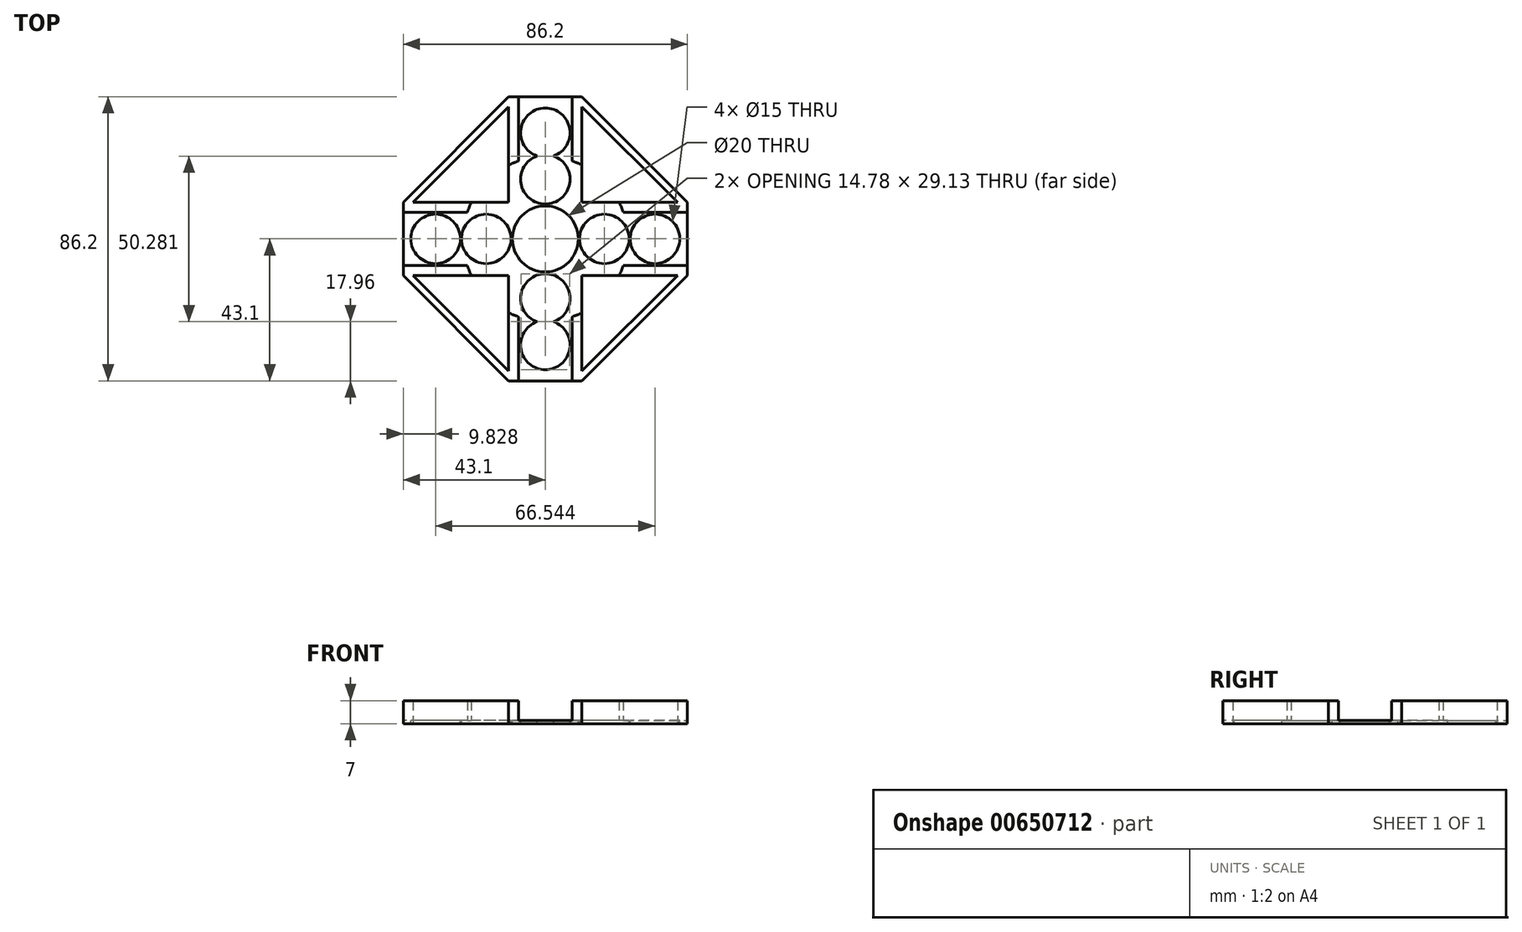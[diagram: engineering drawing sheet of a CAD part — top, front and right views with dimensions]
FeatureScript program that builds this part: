
annotation { "Feature Type Name" : "Feature", "Feature Type Description" : "" }
export const myFeature = defineFeature(function(context is Context, id is Id, definition is map)
    precondition{}
    {
        {
            var Q0;
            Q0=qCreatedBy(makeId("Top.planeOp"),FACE);
            var sketch = newSketch(context, id + "F0", { "sketchPlane" : qUnion([Q0])});
            skLineSegment(sketch, "E0.bottom", {"start": v(8.1, -64.67) * mm, "end": v(-8.1, -64.67) * mm, "construction": true});
            skLineSegment(sketch, "E0.top", {"start": v(8.1, 64.67) * mm, "end": v(-8.1, 64.67) * mm, "construction": true});
            skLineSegment(sketch, "E0.left", {"start": v(8.1, -64.67) * mm, "end": v(8.1, 64.67) * mm, "construction": true});
            skLineSegment(sketch, "E0.right", {"start": v(-8.1, -64.67) * mm, "end": v(-8.1, 64.67) * mm, "construction": true});
            skPoint(sketch, "E0.middle", {"position": v(0, 0) * mm});
            skLineSegment(sketch, "E1.bottom", {"start": v(98.4, -8.1) * mm, "end": v(-98.4, -8.1) * mm, "construction": true});
            skLineSegment(sketch, "E1.top", {"start": v(98.4, 8.1) * mm, "end": v(-98.4, 8.1) * mm, "construction": true});
            skLineSegment(sketch, "E1.left", {"start": v(98.4, -8.1) * mm, "end": v(98.4, 8.1) * mm, "construction": true});
            skLineSegment(sketch, "E1.right", {"start": v(-98.4, -8.1) * mm, "end": v(-98.4, 8.1) * mm, "construction": true});
            skLineSegment(sketch, "E2.bottom", {"start": v(11.1, -18.1) * mm, "end": v(-11.1, -18.1) * mm});
            skLineSegment(sketch, "E2.top", {"start": v(11.1, 18.1) * mm, "end": v(-11.1, 18.1) * mm});
            skLineSegment(sketch, "E2.left", {"start": v(11.1, -18.1) * mm, "end": v(11.1, -11.1) * mm});
            skLineSegment(sketch, "E2.right", {"start": v(-11.1, -18.1) * mm, "end": v(-11.1, -11.1) * mm});
            skLineSegment(sketch, "E3.bottom", {"start": v(18.1, -11.1) * mm, "end": v(11.1, -11.1) * mm});
            skLineSegment(sketch, "E3.top", {"start": v(18.1, 11.1) * mm, "end": v(11.1, 11.1) * mm});
            skLineSegment(sketch, "E3.left", {"start": v(18.1, -11.1) * mm, "end": v(18.1, 11.1) * mm});
            skLineSegment(sketch, "E3.right", {"start": v(-18.1, -11.1) * mm, "end": v(-18.1, 11.1) * mm});
            skLineSegment(sketch, "E4.trimOffspring", {"start": v(-11.1, 11.1) * mm, "end": v(-11.1, 18.1) * mm});
            skLineSegment(sketch, "E5.trimOffspring", {"start": v(11.1, 11.1) * mm, "end": v(11.1, 18.1) * mm});
            skLineSegment(sketch, "E6.trimOffspring", {"start": v(-11.1, -11.1) * mm, "end": v(-18.1, -11.1) * mm});
            skLineSegment(sketch, "E7.trimOffspring", {"start": v(-11.1, 11.1) * mm, "end": v(-18.1, 11.1) * mm});
            skSolve(sketch);
        }
        {
            var Q0;
            Q0 = qSketchRegion(id + "F0", true);
            var Q1;
            Q1=makeQuery(id+"F0.imprint","IMPRINT",FACE,{"disambiguationData":[TD([[makeQuery(id+"F0.imprint","IMPRINT",EDGE,{"derivedFrom":sQuery(id+"F0.wireOp",EDGE,"E2.bottom")}),-1.0]])]});
            extrude(context, id + "F1", {"entities" : qUnion([Q0, Q1]), "depth" : 1 * mm, "offsetDistance" : 25 * mm});
        }
        {
            var Q0;
            Q0=makeQuery(id+"F1.opExtrude","CAP_FACE",FACE,{"disambiguationData":[OSD([sQuery(id+"F0.wireOp",EDGE,"E2.bottom"),sQuery(id+"F0.wireOp",EDGE,"E2.top"),sQuery(id+"F0.wireOp",EDGE,"E2.left"),sQuery(id+"F0.wireOp",EDGE,"E2.right"),sQuery(id+"F0.wireOp",EDGE,"E3.bottom"),sQuery(id+"F0.wireOp",EDGE,"E3.top"),sQuery(id+"F0.wireOp",EDGE,"E3.left"),sQuery(id+"F0.wireOp",EDGE,"E3.right"),sQuery(id+"F0.wireOp",EDGE,"E4.trimOffspring"),sQuery(id+"F0.wireOp",EDGE,"E5.trimOffspring"),sQuery(id+"F0.wireOp",EDGE,"E6.trimOffspring"),sQuery(id+"F0.wireOp",EDGE,"E7.trimOffspring")])],"isStart":false});
            var sketch = newSketch(context, id + "F2", { "sketchPlane" : qUnion([Q0])});
            skLineSegment(sketch, "E8.0", {"start": v(-8.1, -64.67) * mm, "end": v(-8.1, 64.67) * mm, "construction": true});
            skLineSegment(sketch, "E8.1", {"start": v(98.4, 8.1) * mm, "end": v(-98.4, 8.1) * mm, "construction": true});
            skLineSegment(sketch, "E8.2", {"start": v(98.4, -8.1) * mm, "end": v(-98.4, -8.1) * mm, "construction": true});
            skLineSegment(sketch, "E8.3", {"start": v(8.1, -64.67) * mm, "end": v(8.1, 64.67) * mm, "construction": true});
            skLineSegment(sketch, "E9", {"start": v(-8.1, 8.1) * mm, "end": v(-8.1, 18.1) * mm});
            skLineSegment(sketch, "E10", {"start": v(-8.1, 8.1) * mm, "end": v(-18.1, 8.1) * mm});
            skLineSegment(sketch, "E11", {"start": v(8.1, 8.1) * mm, "end": v(18.1, 8.1) * mm});
            skLineSegment(sketch, "E12", {"start": v(8.1, 18.1) * mm, "end": v(8.1, 8.1) * mm});
            skLineSegment(sketch, "E13", {"start": v(-8.1, -8.1) * mm, "end": v(-8.1, -18.1) * mm});
            skLineSegment(sketch, "E14", {"start": v(-18.1, -8.1) * mm, "end": v(-8.1, -8.1) * mm});
            skLineSegment(sketch, "E15", {"start": v(8.1, -8.1) * mm, "end": v(18.1, -8.1) * mm});
            skLineSegment(sketch, "E16", {"start": v(8.1, -8.1) * mm, "end": v(8.1, -18.1) * mm});
            skSolve(sketch);
        }
        {
            var Q0;
            {var subQ4=sQuery(id+"F2.wireOp",EDGE,"E9");Q0=makeQuery(id+"F2.imprint","IMPRINT",FACE,{"disambiguationData":[TD([[makeQuery(id+"F2.imprint","IMPRINT",EDGE,{"derivedFrom":subQ4}),1.0]])]});}
            var Q1;
            {var subQ2=sQuery(id+"F2.wireOp",EDGE,"E11");Q1=makeQuery(id+"F2.imprint","IMPRINT",FACE,{"disambiguationData":[TD([[makeQuery(id+"F2.imprint","IMPRINT",EDGE,{"derivedFrom":subQ2}),1.0]])]});}
            var Q2;
            {var subQ3=sQuery(id+"F2.wireOp",EDGE,"E15");Q2=makeQuery(id+"F2.imprint","IMPRINT",FACE,{"disambiguationData":[TD([[makeQuery(id+"F2.imprint","IMPRINT",EDGE,{"derivedFrom":subQ3}),-1.0]])]});}
            var Q3;
            {var subQ4=sQuery(id+"F2.wireOp",EDGE,"E13");Q3=makeQuery(id+"F2.imprint","IMPRINT",FACE,{"disambiguationData":[TD([[makeQuery(id+"F2.imprint","IMPRINT",EDGE,{"derivedFrom":subQ4}),-1.0]])]});}
            extrude(context, id + "F3", {"entities" : qUnion([Q0, Q1, Q2, Q3]), "operationType" : NewBodyOperationType.ADD, "depth" : 6 * mm, "offsetDistance" : 25 * mm});
        }
        {
            var Q0;
            {var subQ0=sQuery(id+"F0.wireOp",EDGE,"E3.right");var subQ1=makeQuery(id+"F1.opExtrude","CAP_EDGE",EDGE,{"disambiguationData":[OSD([subQ0])],"isStart":false});Q0=makeQuery(id+"F3.boolean.opBoolean","MERGE",FACE,{"derivedFrom":[makeQuery(id+"F1.opExtrude","SWEPT_FACE",FACE,{"disambiguationData":[OSD([subQ0])]}),makeQuery(id+"F3.opExtrude","SWEPT_FACE",FACE,{"disambiguationData":[OSD([subQ0]),TDD([makeQuery(id+"F2.imprint","IMPRINT",EDGE,{"disambiguationData":[TD([[makeQuery(id+"F2.imprint","INTERSECT",VERTEX,{"derivedFrom":[subQ1,makeQuery(id+"F1.opExtrude","CAP_EDGE",EDGE,{"disambiguationData":[OSD([sQuery(id+"F0.wireOp",EDGE,"E6.trimOffspring")])],"isStart":false})]}),-1.0]])],"derivedFrom":subQ1})])]}),makeQuery(id+"F3.opExtrude","SWEPT_FACE",FACE,{"disambiguationData":[OSD([subQ0]),TDD([makeQuery(id+"F2.imprint","IMPRINT",EDGE,{"disambiguationData":[TD([[makeQuery(id+"F2.imprint","INTERSECT",VERTEX,{"derivedFrom":[subQ1,makeQuery(id+"F1.opExtrude","CAP_EDGE",EDGE,{"disambiguationData":[OSD([sQuery(id+"F0.wireOp",EDGE,"E7.trimOffspring")])],"isStart":false})]}),1.0]])],"derivedFrom":subQ1})])]})]});}
            extrude(context, id + "F4", {"entities" : qUnion([Q0]), "operationType" : NewBodyOperationType.ADD, "depth" : 25 * mm, "offsetDistance" : 25 * mm});
        }
        {
            var Q0;
            {var subQ0=sQuery(id+"F0.wireOp",EDGE,"E3.left");var subQ1=makeQuery(id+"F1.opExtrude","CAP_EDGE",EDGE,{"disambiguationData":[OSD([subQ0])],"isStart":false});Q0=makeQuery(id+"F3.boolean.opBoolean","MERGE",FACE,{"derivedFrom":[makeQuery(id+"F1.opExtrude","SWEPT_FACE",FACE,{"disambiguationData":[OSD([subQ0])]}),makeQuery(id+"F3.opExtrude","SWEPT_FACE",FACE,{"disambiguationData":[OSD([subQ0]),TDD([makeQuery(id+"F2.imprint","IMPRINT",EDGE,{"disambiguationData":[TD([[makeQuery(id+"F2.imprint","INTERSECT",VERTEX,{"derivedFrom":[makeQuery(id+"F1.opExtrude","CAP_EDGE",EDGE,{"disambiguationData":[OSD([sQuery(id+"F0.wireOp",EDGE,"E3.bottom")])],"isStart":false}),subQ1]}),-1.0]])],"derivedFrom":subQ1})])]}),makeQuery(id+"F3.opExtrude","SWEPT_FACE",FACE,{"disambiguationData":[OSD([subQ0]),TDD([makeQuery(id+"F2.imprint","IMPRINT",EDGE,{"disambiguationData":[TD([[makeQuery(id+"F2.imprint","INTERSECT",VERTEX,{"derivedFrom":[makeQuery(id+"F1.opExtrude","CAP_EDGE",EDGE,{"disambiguationData":[OSD([sQuery(id+"F0.wireOp",EDGE,"E3.top")])],"isStart":false}),subQ1]}),1.0]])],"derivedFrom":subQ1})])]})]});}
            extrude(context, id + "F5", {"entities" : qUnion([Q0]), "operationType" : NewBodyOperationType.ADD, "depth" : 25 * mm, "offsetDistance" : 25 * mm});
        }
        {
            var Q0;
            {var subQ0=sQuery(id+"F0.wireOp",EDGE,"E2.bottom");var subQ1=makeQuery(id+"F1.opExtrude","CAP_EDGE",EDGE,{"disambiguationData":[OSD([subQ0])],"isStart":false});Q0=makeQuery(id+"F3.boolean.opBoolean","MERGE",FACE,{"derivedFrom":[makeQuery(id+"F1.opExtrude","SWEPT_FACE",FACE,{"disambiguationData":[OSD([subQ0])]}),makeQuery(id+"F3.opExtrude","SWEPT_FACE",FACE,{"disambiguationData":[OSD([subQ0]),TDD([makeQuery(id+"F2.imprint","IMPRINT",EDGE,{"disambiguationData":[TD([[makeQuery(id+"F2.imprint","INTERSECT",VERTEX,{"derivedFrom":[subQ1,makeQuery(id+"F1.opExtrude","CAP_EDGE",EDGE,{"disambiguationData":[OSD([sQuery(id+"F0.wireOp",EDGE,"E2.left")])],"isStart":false})]}),-1.0]])],"derivedFrom":subQ1})])]}),makeQuery(id+"F3.opExtrude","SWEPT_FACE",FACE,{"disambiguationData":[OSD([subQ0]),TDD([makeQuery(id+"F2.imprint","IMPRINT",EDGE,{"disambiguationData":[TD([[makeQuery(id+"F2.imprint","INTERSECT",VERTEX,{"derivedFrom":[subQ1,makeQuery(id+"F1.opExtrude","CAP_EDGE",EDGE,{"disambiguationData":[OSD([sQuery(id+"F0.wireOp",EDGE,"E2.right")])],"isStart":false})]}),1.0]])],"derivedFrom":subQ1})])]})]});}
            extrude(context, id + "F6", {"entities" : qUnion([Q0]), "operationType" : NewBodyOperationType.ADD, "depth" : 25 * mm, "offsetDistance" : 25 * mm});
        }
        {
            var Q0;
            {var subQ0=sQuery(id+"F0.wireOp",EDGE,"E2.top");var subQ1=makeQuery(id+"F1.opExtrude","CAP_EDGE",EDGE,{"disambiguationData":[OSD([subQ0])],"isStart":false});Q0=makeQuery(id+"F3.boolean.opBoolean","MERGE",FACE,{"derivedFrom":[makeQuery(id+"F1.opExtrude","SWEPT_FACE",FACE,{"disambiguationData":[OSD([subQ0])]}),makeQuery(id+"F3.opExtrude","SWEPT_FACE",FACE,{"disambiguationData":[OSD([subQ0]),TDD([makeQuery(id+"F2.imprint","IMPRINT",EDGE,{"disambiguationData":[TD([[makeQuery(id+"F2.imprint","INTERSECT",VERTEX,{"derivedFrom":[subQ1,makeQuery(id+"F1.opExtrude","CAP_EDGE",EDGE,{"disambiguationData":[OSD([sQuery(id+"F0.wireOp",EDGE,"E5.trimOffspring")])],"isStart":false})]}),-1.0]])],"derivedFrom":subQ1})])]}),makeQuery(id+"F3.opExtrude","SWEPT_FACE",FACE,{"disambiguationData":[OSD([subQ0]),TDD([makeQuery(id+"F2.imprint","IMPRINT",EDGE,{"disambiguationData":[TD([[makeQuery(id+"F2.imprint","INTERSECT",VERTEX,{"derivedFrom":[subQ1,makeQuery(id+"F1.opExtrude","CAP_EDGE",EDGE,{"disambiguationData":[OSD([sQuery(id+"F0.wireOp",EDGE,"E4.trimOffspring")])],"isStart":false})]}),1.0]])],"derivedFrom":subQ1})])]})]});}
            extrude(context, id + "F7", {"entities" : qUnion([Q0]), "operationType" : NewBodyOperationType.ADD, "depth" : 25 * mm, "offsetDistance" : 25 * mm});
        }
        {
            var Q0;
            {var subQ0=sQuery(id+"F0.wireOp",EDGE,"E2.top");var subQ1=sQuery(id+"F0.wireOp",EDGE,"E2.bottom");var subQ2=sQuery(id+"F0.wireOp",EDGE,"E3.left");var subQ3=sQuery(id+"F0.wireOp",EDGE,"E3.right");Q0=makeQuery(id+"F7.boolean.opBoolean","MERGE",FACE,{"derivedFrom":[makeQuery(id+"F6.boolean.opBoolean","MERGE",FACE,{"derivedFrom":[makeQuery(id+"F5.boolean.opBoolean","MERGE",FACE,{"derivedFrom":[makeQuery(id+"F4.boolean.opBoolean","MERGE",FACE,{"derivedFrom":[makeQuery(id+"F1.opExtrude","CAP_FACE",FACE,{"disambiguationData":[OSD([subQ1,subQ0,sQuery(id+"F0.wireOp",EDGE,"E2.left"),sQuery(id+"F0.wireOp",EDGE,"E2.right"),sQuery(id+"F0.wireOp",EDGE,"E3.bottom"),sQuery(id+"F0.wireOp",EDGE,"E3.top"),subQ2,subQ3,sQuery(id+"F0.wireOp",EDGE,"E4.trimOffspring"),sQuery(id+"F0.wireOp",EDGE,"E5.trimOffspring"),sQuery(id+"F0.wireOp",EDGE,"E6.trimOffspring"),sQuery(id+"F0.wireOp",EDGE,"E7.trimOffspring")])],"isStart":false}),makeQuery(id+"F4.opExtrude","SWEPT_FACE",FACE,{"disambiguationData":[OSD([subQ3]),TDD([makeQuery(id+"F1.opExtrude","CAP_EDGE",EDGE,{"disambiguationData":[OSD([subQ3])],"isStart":false})])]})]}),makeQuery(id+"F5.opExtrude","SWEPT_FACE",FACE,{"disambiguationData":[OSD([subQ2]),TDD([makeQuery(id+"F1.opExtrude","CAP_EDGE",EDGE,{"disambiguationData":[OSD([subQ2])],"isStart":false})])]})]}),makeQuery(id+"F6.opExtrude","SWEPT_FACE",FACE,{"disambiguationData":[OSD([subQ1]),TDD([makeQuery(id+"F1.opExtrude","CAP_EDGE",EDGE,{"disambiguationData":[OSD([subQ1])],"isStart":false})])]})]}),makeQuery(id+"F7.opExtrude","SWEPT_FACE",FACE,{"disambiguationData":[OSD([subQ0]),TDD([makeQuery(id+"F1.opExtrude","CAP_EDGE",EDGE,{"disambiguationData":[OSD([subQ0])],"isStart":false})])]})]});}
            var sketch = newSketch(context, id + "F8", { "sketchPlane" : qUnion([Q0])});
            skLineSegment(sketch, "E17", {"start": v(0, 0) * mm, "end": v(0, -67.04) * mm, "construction": true});
            skPoint(sketch, "E17.endSnap0", {"position": v(0, -43.1) * mm});
            skLineSegment(sketch, "E18", {"start": v(0, -67.04) * mm, "end": v(0, 0) * mm, "construction": true});
            skLineSegment(sketch, "E19", {"start": v(0, 0) * mm, "end": v(0, 64.4) * mm, "construction": true});
            skLineSegment(sketch, "E20", {"start": v(0, 0) * mm, "end": v(-53.55, 0) * mm, "construction": true});
            skLineSegment(sketch, "E21", {"start": v(0, 0) * mm, "end": v(58.6, 0) * mm, "construction": true});
            skPoint(sketch, "E21.endSnap0", {"position": v(43.1, 0) * mm});
            skLineSegment(sketch, "E22", {"start": v(0, 18.08) * mm, "end": v(-8.1, 18.08) * mm, "construction": true});
            skLineSegment(sketch, "E23", {"start": v(0, 32.2) * mm, "end": v(-8.1, 32.2) * mm, "construction": true});
            skLineSegment(sketch, "E24.MirrorCS", {"start": v(0, -32.2) * mm, "end": v(-8.1, -32.2) * mm, "construction": true});
            skLineSegment(sketch, "E25.MirrorCS", {"start": v(0, -18.08) * mm, "end": v(-8.1, -18.08) * mm, "construction": true});
            skLineSegment(sketch, "E26", {"start": v(-33.27, 0) * mm, "end": v(-33.27, 8.1) * mm, "construction": true});
            skLineSegment(sketch, "E27", {"start": v(-17.9, 0) * mm, "end": v(-17.9, 8.1) * mm, "construction": true});
            skLineSegment(sketch, "E28.MirrorCS", {"start": v(-48.64, 0) * mm, "end": v(-48.64, 8.1) * mm, "construction": true});
            skLineSegment(sketch, "E29.MirrorCS", {"start": v(-66.54, 0) * mm, "end": v(-66.54, 64.4) * mm, "construction": true});
            skLineSegment(sketch, "E30.MirrorCS", {"start": v(33.27, 0) * mm, "end": v(33.27, 8.1) * mm, "construction": true});
            skLineSegment(sketch, "E31.MirrorCS", {"start": v(17.9, 0) * mm, "end": v(17.9, 8.1) * mm, "construction": true});
            skSolve(sketch);
        }
        {
            var Q0;
            Q0=sQuery(id+"F8.wireOp",VERTEX,"E25.MirrorCS.start");
            var Q1;
            Q1=sQuery(id+"F8.wireOp",VERTEX,"E24.MirrorCS.start");
            var Q2;
            Q2=sQuery(id+"F8.wireOp",VERTEX,"E27.start");
            var Q3;
            Q3=sQuery(id+"F8.wireOp",VERTEX,"E26.start");
            var Q4;
            Q4=sQuery(id+"F8.wireOp",VERTEX,"E22.start");
            var Q5;
            Q5=sQuery(id+"F8.wireOp",VERTEX,"E23.start");
            var Q6;
            Q6=sQuery(id+"F8.wireOp",VERTEX,"E30.MirrorCS.start");
            var Q7;
            Q7=sQuery(id+"F8.wireOp",VERTEX,"E31.MirrorCS.start");
            var Q8;
            Q8=makeQuery(id+"F1.opExtrude","SWEPT_BODY",BODY,{"disambiguationData":[OSD([sQuery(id+"F0.wireOp",EDGE,"E2.bottom"),sQuery(id+"F0.wireOp",EDGE,"E2.top"),sQuery(id+"F0.wireOp",EDGE,"E2.left"),sQuery(id+"F0.wireOp",EDGE,"E2.right"),sQuery(id+"F0.wireOp",EDGE,"E3.bottom"),sQuery(id+"F0.wireOp",EDGE,"E3.top"),sQuery(id+"F0.wireOp",EDGE,"E3.left"),sQuery(id+"F0.wireOp",EDGE,"E3.right"),sQuery(id+"F0.wireOp",EDGE,"E4.trimOffspring"),sQuery(id+"F0.wireOp",EDGE,"E5.trimOffspring"),sQuery(id+"F0.wireOp",EDGE,"E6.trimOffspring"),sQuery(id+"F0.wireOp",EDGE,"E7.trimOffspring")])]});
            hole(context, id + "F9", {"style" : HoleStyle.SIMPLE, "endStyle" : HoleEndStyle.THROUGH, "holeDiameter" : 15 * mm, "majorDiameter" : 5 * mm, "isTappedThrough" : true, "tappedDepth" : 12 * mm, "tapClearance" : 3, "locations" : qUnion([Q0, Q1, Q2, Q3, Q4, Q5, Q6, Q7]), "scope" : qUnion([Q8])});
        }
        {
            var Q0;
            {var subQ0=sQuery(id+"F0.wireOp",EDGE,"E6.trimOffspring");Q0=makeQuery(id+"F4.boolean.opBoolean","MERGE",FACE,{"derivedFrom":[makeQuery(id+"F3.boolean.opBoolean","MERGE",FACE,{"derivedFrom":[makeQuery(id+"F1.opExtrude","SWEPT_FACE",FACE,{"disambiguationData":[OSD([subQ0])]}),makeQuery(id+"F3.opExtrude","SWEPT_FACE",FACE,{"disambiguationData":[OSD([subQ0])]})]}),makeQuery(id+"F4.opExtrude","SWEPT_FACE",FACE,{"disambiguationData":[OSD([sQuery(id+"F0.wireOp",EDGE,"E3.right"),subQ0])]})]});}
            var sketch = newSketch(context, id + "F10", { "sketchPlane" : qUnion([Q0])});
            skLineSegment(sketch, "E32.0", {"start": v(-43.1, 7) * mm, "end": v(-43.1, 0) * mm});
            skLineSegment(sketch, "E33.0", {"start": v(-11.1, 7) * mm, "end": v(-43.1, 7) * mm});
            skLineSegment(sketch, "E34.0", {"start": v(-11.1, 0) * mm, "end": v(-43.1, 0) * mm});
            skLineSegment(sketch, "E35", {"start": v(-40.1, 7) * mm, "end": v(-40.1, 0) * mm});
            skSolve(sketch);
        }
        {
            var Q0;
            {var subQ0=sQuery(id+"F0.wireOp",EDGE,"E2.right");Q0=makeQuery(id+"F6.boolean.opBoolean","MERGE",FACE,{"derivedFrom":[makeQuery(id+"F3.boolean.opBoolean","MERGE",FACE,{"derivedFrom":[makeQuery(id+"F1.opExtrude","SWEPT_FACE",FACE,{"disambiguationData":[OSD([subQ0])]}),makeQuery(id+"F3.opExtrude","SWEPT_FACE",FACE,{"disambiguationData":[OSD([subQ0])]})]}),makeQuery(id+"F6.opExtrude","SWEPT_FACE",FACE,{"disambiguationData":[OSD([sQuery(id+"F0.wireOp",EDGE,"E2.bottom"),subQ0])]})]});}
            var sketch = newSketch(context, id + "F11", { "sketchPlane" : qUnion([Q0])});
            skLineSegment(sketch, "E36.0", {"start": v(43.1, 0) * mm, "end": v(11.1, 0) * mm});
            skLineSegment(sketch, "E36.1", {"start": v(43.1, 7) * mm, "end": v(43.1, 0) * mm});
            skLineSegment(sketch, "E36.3", {"start": v(43.1, 7) * mm, "end": v(11.1, 7) * mm});
            skLineSegment(sketch, "E37", {"start": v(40.1, 7) * mm, "end": v(40.1, 0) * mm});
            skSolve(sketch);
        }
        {
            var Q0;
            {var subQ0=sQuery(id+"F0.wireOp",EDGE,"E3.bottom");Q0=makeQuery(id+"F5.boolean.opBoolean","MERGE",FACE,{"derivedFrom":[makeQuery(id+"F3.boolean.opBoolean","MERGE",FACE,{"derivedFrom":[makeQuery(id+"F1.opExtrude","SWEPT_FACE",FACE,{"disambiguationData":[OSD([subQ0])]}),makeQuery(id+"F3.opExtrude","SWEPT_FACE",FACE,{"disambiguationData":[OSD([subQ0])]})]}),makeQuery(id+"F5.opExtrude","SWEPT_FACE",FACE,{"disambiguationData":[OSD([subQ0,sQuery(id+"F0.wireOp",EDGE,"E3.left")])]})]});}
            var sketch = newSketch(context, id + "F12", { "sketchPlane" : qUnion([Q0])});
            skLineSegment(sketch, "E38.0", {"start": v(43.1, 7) * mm, "end": v(11.1, 7) * mm});
            skLineSegment(sketch, "E39", {"start": v(40.1, 7) * mm, "end": v(40.1, 0) * mm});
            skLineSegment(sketch, "E40.0", {"start": v(43.1, 7) * mm, "end": v(43.1, 0) * mm});
            skLineSegment(sketch, "E41.0", {"start": v(43.1, 0) * mm, "end": v(11.1, 0) * mm});
            skSolve(sketch);
        }
        {
            var Q0;
            {var subQ0=sQuery(id+"F0.wireOp",EDGE,"E2.left");Q0=makeQuery(id+"F6.boolean.opBoolean","MERGE",FACE,{"derivedFrom":[makeQuery(id+"F3.boolean.opBoolean","MERGE",FACE,{"derivedFrom":[makeQuery(id+"F1.opExtrude","SWEPT_FACE",FACE,{"disambiguationData":[OSD([subQ0])]}),makeQuery(id+"F3.opExtrude","SWEPT_FACE",FACE,{"disambiguationData":[OSD([subQ0])]})]}),makeQuery(id+"F6.opExtrude","SWEPT_FACE",FACE,{"disambiguationData":[OSD([sQuery(id+"F0.wireOp",EDGE,"E2.bottom"),subQ0])]})]});}
            var sketch = newSketch(context, id + "F13", { "sketchPlane" : qUnion([Q0])});
            skLineSegment(sketch, "E42.0", {"start": v(-43.1, 7) * mm, "end": v(-11.1, 7) * mm});
            skLineSegment(sketch, "E42.1", {"start": v(-43.1, 0) * mm, "end": v(-11.1, 0) * mm});
            skLineSegment(sketch, "E42.2", {"start": v(-43.1, 7) * mm, "end": v(-43.1, 0) * mm});
            skLineSegment(sketch, "E43", {"start": v(-40.1, 7) * mm, "end": v(-40.1, 0) * mm});
            skSolve(sketch);
        }
        {
            var Q0;
            {var subQ0=sQuery(id+"F0.wireOp",EDGE,"E3.top");Q0=makeQuery(id+"F5.boolean.opBoolean","MERGE",FACE,{"derivedFrom":[makeQuery(id+"F3.boolean.opBoolean","MERGE",FACE,{"derivedFrom":[makeQuery(id+"F1.opExtrude","SWEPT_FACE",FACE,{"disambiguationData":[OSD([subQ0])]}),makeQuery(id+"F3.opExtrude","SWEPT_FACE",FACE,{"disambiguationData":[OSD([subQ0])]})]}),makeQuery(id+"F5.opExtrude","SWEPT_FACE",FACE,{"disambiguationData":[OSD([subQ0,sQuery(id+"F0.wireOp",EDGE,"E3.left")])]})]});}
            var sketch = newSketch(context, id + "F14", { "sketchPlane" : qUnion([Q0])});
            skLineSegment(sketch, "E44.0", {"start": v(-43.1, 7) * mm, "end": v(-11.1, 7) * mm});
            skLineSegment(sketch, "E44.1", {"start": v(-43.1, 7) * mm, "end": v(-43.1, 0) * mm});
            skLineSegment(sketch, "E44.2", {"start": v(-43.1, 0) * mm, "end": v(-11.1, 0) * mm});
            skLineSegment(sketch, "E45", {"start": v(-40.1, 0) * mm, "end": v(-40.1, 7) * mm});
            skLineSegment(sketch, "E46.1", {"start": v(-11.1, 7) * mm, "end": v(-11.1, 0) * mm});
            skSolve(sketch);
        }
        {
            var Q0;
            {var subQ0=sQuery(id+"F0.wireOp",EDGE,"E5.trimOffspring");Q0=makeQuery(id+"F7.boolean.opBoolean","MERGE",FACE,{"derivedFrom":[makeQuery(id+"F3.boolean.opBoolean","MERGE",FACE,{"derivedFrom":[makeQuery(id+"F1.opExtrude","SWEPT_FACE",FACE,{"disambiguationData":[OSD([subQ0])]}),makeQuery(id+"F3.opExtrude","SWEPT_FACE",FACE,{"disambiguationData":[OSD([subQ0])]})]}),makeQuery(id+"F7.opExtrude","SWEPT_FACE",FACE,{"disambiguationData":[OSD([sQuery(id+"F0.wireOp",EDGE,"E2.top"),subQ0])]})]});}
            var sketch = newSketch(context, id + "F15", { "sketchPlane" : qUnion([Q0])});
            skLineSegment(sketch, "E47.0", {"start": v(11.1, 7) * mm, "end": v(43.1, 7) * mm});
            skLineSegment(sketch, "E47.1", {"start": v(43.1, 7) * mm, "end": v(43.1, 0) * mm});
            skLineSegment(sketch, "E47.2", {"start": v(11.1, 0) * mm, "end": v(43.1, 0) * mm});
            skLineSegment(sketch, "E48", {"start": v(40.1, 7) * mm, "end": v(40.1, 0) * mm});
            skSolve(sketch);
        }
        {
            var Q0;
            {var subQ0=sQuery(id+"F0.wireOp",EDGE,"E4.trimOffspring");Q0=makeQuery(id+"F7.boolean.opBoolean","MERGE",FACE,{"derivedFrom":[makeQuery(id+"F3.boolean.opBoolean","MERGE",FACE,{"derivedFrom":[makeQuery(id+"F1.opExtrude","SWEPT_FACE",FACE,{"disambiguationData":[OSD([subQ0])]}),makeQuery(id+"F3.opExtrude","SWEPT_FACE",FACE,{"disambiguationData":[OSD([subQ0])]})]}),makeQuery(id+"F7.opExtrude","SWEPT_FACE",FACE,{"disambiguationData":[OSD([sQuery(id+"F0.wireOp",EDGE,"E2.top"),subQ0])]})]});}
            var sketch = newSketch(context, id + "F16", { "sketchPlane" : qUnion([Q0])});
            skLineSegment(sketch, "E49.0", {"start": v(-11.1, 7) * mm, "end": v(-43.1, 7) * mm});
            skLineSegment(sketch, "E49.1", {"start": v(-43.1, 7) * mm, "end": v(-43.1, 0) * mm});
            skLineSegment(sketch, "E49.2", {"start": v(-11.1, 0) * mm, "end": v(-43.1, 0) * mm});
            skLineSegment(sketch, "E50", {"start": v(-40.1, 0) * mm, "end": v(-40.1, 7) * mm});
            skSolve(sketch);
        }
        {
            var Q0;
            {var subQ0=sQuery(id+"F0.wireOp",EDGE,"E7.trimOffspring");Q0=makeQuery(id+"F4.boolean.opBoolean","MERGE",FACE,{"derivedFrom":[makeQuery(id+"F3.boolean.opBoolean","MERGE",FACE,{"derivedFrom":[makeQuery(id+"F1.opExtrude","SWEPT_FACE",FACE,{"disambiguationData":[OSD([subQ0])]}),makeQuery(id+"F3.opExtrude","SWEPT_FACE",FACE,{"disambiguationData":[OSD([subQ0])]})]}),makeQuery(id+"F4.opExtrude","SWEPT_FACE",FACE,{"disambiguationData":[OSD([sQuery(id+"F0.wireOp",EDGE,"E3.right"),subQ0])]})]});}
            var sketch = newSketch(context, id + "F17", { "sketchPlane" : qUnion([Q0])});
            skLineSegment(sketch, "E51.0", {"start": v(11.1, 7) * mm, "end": v(43.1, 7) * mm});
            skLineSegment(sketch, "E51.1", {"start": v(43.1, 7) * mm, "end": v(43.1, 0) * mm});
            skLineSegment(sketch, "E51.2", {"start": v(11.1, 0) * mm, "end": v(43.1, 0) * mm});
            skLineSegment(sketch, "E52", {"start": v(40.1, 7) * mm, "end": v(40.1, 0) * mm});
            skSolve(sketch);
        }
        {
            var Q1;
            {var subQ0=sQuery(id+"F10.wireOp",EDGE,"E32.0");Q1=makeQuery(id+"F10.imprint","IMPRINT",FACE,{"disambiguationData":[TD([[makeQuery(id+"F10.imprint","IMPRINT",EDGE,{"derivedFrom":subQ0}),1.0]])]});}
            var Q2;
            {var subQ0=sQuery(id+"F11.wireOp",EDGE,"E36.1");Q2=makeQuery(id+"F11.imprint","IMPRINT",FACE,{"disambiguationData":[TD([[makeQuery(id+"F11.imprint","IMPRINT",EDGE,{"derivedFrom":subQ0}),-1.0]])]});}
            loft(context, id + "F18", {"operationType" : NewBodyOperationType.ADD, "sheetProfilesArray" : [{ "sheetProfileEntities" : qUnion([Q1]) }, { "sheetProfileEntities" : qUnion([Q2]) }]});
        }
        {
            var Q1;
            {var subQ0=sQuery(id+"F16.wireOp",EDGE,"E49.1");Q1=makeQuery(id+"F16.imprint","IMPRINT",FACE,{"disambiguationData":[TD([[makeQuery(id+"F16.imprint","IMPRINT",EDGE,{"derivedFrom":subQ0}),1.0]])]});}
            var Q2;
            {var subQ0=sQuery(id+"F17.wireOp",EDGE,"E51.1");Q2=makeQuery(id+"F17.imprint","IMPRINT",FACE,{"disambiguationData":[TD([[makeQuery(id+"F17.imprint","IMPRINT",EDGE,{"derivedFrom":subQ0}),-1.0]])]});}
            loft(context, id + "F19", {"operationType" : NewBodyOperationType.ADD, "sheetProfilesArray" : [{ "sheetProfileEntities" : qUnion([Q1]) }, { "sheetProfileEntities" : qUnion([Q2]) }]});
        }
        {
            var Q1;
            {var subQ0=sQuery(id+"F15.wireOp",EDGE,"E47.1");Q1=makeQuery(id+"F15.imprint","IMPRINT",FACE,{"disambiguationData":[TD([[makeQuery(id+"F15.imprint","IMPRINT",EDGE,{"derivedFrom":subQ0}),-1.0]])]});}
            var Q2;
            {var subQ0=sQuery(id+"F14.wireOp",EDGE,"E44.1");Q2=makeQuery(id+"F14.imprint","IMPRINT",FACE,{"disambiguationData":[TD([[makeQuery(id+"F14.imprint","IMPRINT",EDGE,{"derivedFrom":subQ0}),1.0]])]});}
            loft(context, id + "F20", {"operationType" : NewBodyOperationType.ADD, "sheetProfilesArray" : [{ "sheetProfileEntities" : qUnion([Q1]) }, { "sheetProfileEntities" : qUnion([Q2]) }]});
        }
        {
            var Q1;
            {var subQ2=sQuery(id+"F12.wireOp",EDGE,"E39");Q1=makeQuery(id+"F12.imprint","IMPRINT",FACE,{"disambiguationData":[TD([[makeQuery(id+"F12.imprint","IMPRINT",EDGE,{"derivedFrom":subQ2}),1.0]])]});}
            var Q2;
            {var subQ0=sQuery(id+"F13.wireOp",EDGE,"E42.2");Q2=makeQuery(id+"F13.imprint","IMPRINT",FACE,{"disambiguationData":[TD([[makeQuery(id+"F13.imprint","IMPRINT",EDGE,{"derivedFrom":subQ0}),1.0]])]});}
            loft(context, id + "F21", {"operationType" : NewBodyOperationType.ADD, "sheetProfilesArray" : [{ "sheetProfileEntities" : qUnion([Q1]) }, { "sheetProfileEntities" : qUnion([Q2]) }]});
        }
        {
            var Q0;
            Q0=sQuery(id+"F8.wireOp",VERTEX,"E17.start");
            var Q1;
            Q1=makeQuery(id+"F1.opExtrude","SWEPT_BODY",BODY,{"disambiguationData":[OSD([sQuery(id+"F0.wireOp",EDGE,"E2.bottom"),sQuery(id+"F0.wireOp",EDGE,"E2.top"),sQuery(id+"F0.wireOp",EDGE,"E2.left"),sQuery(id+"F0.wireOp",EDGE,"E2.right"),sQuery(id+"F0.wireOp",EDGE,"E3.bottom"),sQuery(id+"F0.wireOp",EDGE,"E3.top"),sQuery(id+"F0.wireOp",EDGE,"E3.left"),sQuery(id+"F0.wireOp",EDGE,"E3.right"),sQuery(id+"F0.wireOp",EDGE,"E4.trimOffspring"),sQuery(id+"F0.wireOp",EDGE,"E5.trimOffspring"),sQuery(id+"F0.wireOp",EDGE,"E6.trimOffspring"),sQuery(id+"F0.wireOp",EDGE,"E7.trimOffspring")])]});
            hole(context, id + "F22", {"style" : HoleStyle.SIMPLE, "endStyle" : HoleEndStyle.THROUGH, "oppositeDirection" : true, "holeDiameter" : 50 * mm, "majorDiameter" : 5 * mm, "isTappedThrough" : true, "tappedDepth" : 12 * mm, "tapClearance" : 3, "locations" : qUnion([Q0]), "scope" : qUnion([Q1])});
        }
        {
            var Q0;
            Q0=sQuery(id+"F8.wireOp",VERTEX,"E17.start");
            var Q1;
            Q1=makeQuery(id+"F1.opExtrude","SWEPT_BODY",BODY,{"disambiguationData":[OSD([sQuery(id+"F0.wireOp",EDGE,"E2.bottom"),sQuery(id+"F0.wireOp",EDGE,"E2.top"),sQuery(id+"F0.wireOp",EDGE,"E2.left"),sQuery(id+"F0.wireOp",EDGE,"E2.right"),sQuery(id+"F0.wireOp",EDGE,"E3.bottom"),sQuery(id+"F0.wireOp",EDGE,"E3.top"),sQuery(id+"F0.wireOp",EDGE,"E3.left"),sQuery(id+"F0.wireOp",EDGE,"E3.right"),sQuery(id+"F0.wireOp",EDGE,"E4.trimOffspring"),sQuery(id+"F0.wireOp",EDGE,"E5.trimOffspring"),sQuery(id+"F0.wireOp",EDGE,"E6.trimOffspring"),sQuery(id+"F0.wireOp",EDGE,"E7.trimOffspring")])]});
            hole(context, id + "F23", {"style" : HoleStyle.SIMPLE, "endStyle" : HoleEndStyle.THROUGH, "holeDiameter" : 20 * mm, "majorDiameter" : 5 * mm, "isTappedThrough" : true, "tappedDepth" : 12 * mm, "tapClearance" : 3, "locations" : qUnion([Q0]), "scope" : qUnion([Q1])});
        }
    });
